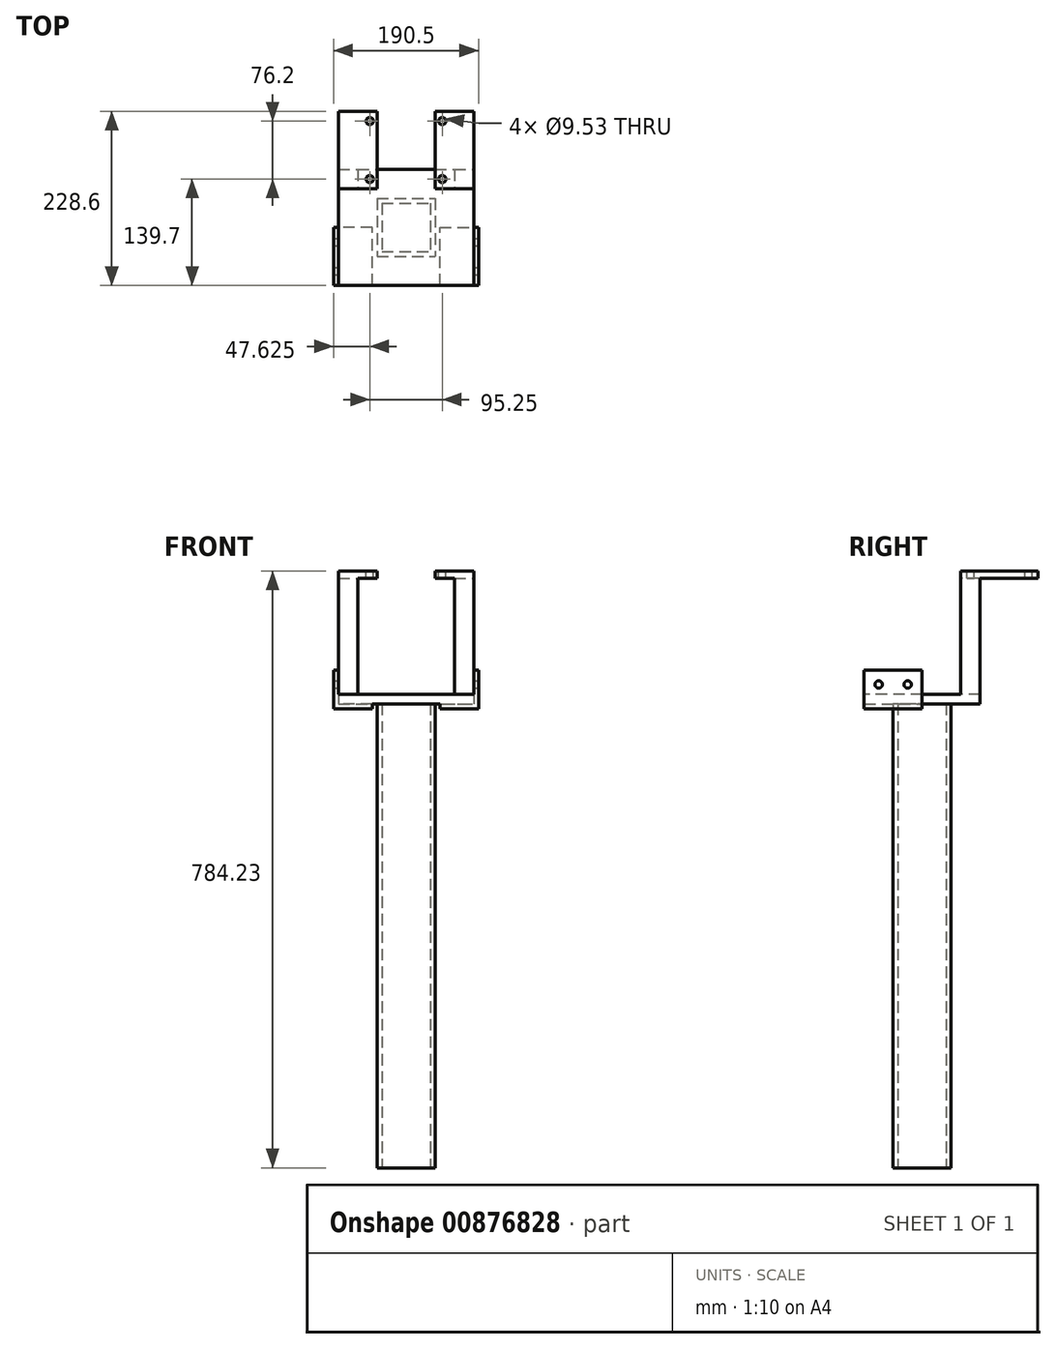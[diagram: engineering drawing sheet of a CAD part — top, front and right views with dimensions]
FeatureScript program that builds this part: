
annotation { "Feature Type Name" : "Feature", "Feature Type Description" : "" }
export const myFeature = defineFeature(function(context is Context, id is Id, definition is map)
    precondition{}
    {
        {
            var Q0;
            Q0=qCreatedBy(makeId("Top.planeOp"),FACE);
            var sketch = newSketch(context, id + "F0", { "sketchPlane" : qUnion([Q0])});
            skLineSegment(sketch, "E0.bottom", {"start": v(-38.1, 38.1) * mm, "end": v(38.1, 38.1) * mm});
            skLineSegment(sketch, "E0.top", {"start": v(-38.1, -38.1) * mm, "end": v(38.1, -38.1) * mm});
            skLineSegment(sketch, "E0.left", {"start": v(-38.1, 38.1) * mm, "end": v(-38.1, -38.1) * mm});
            skLineSegment(sketch, "E0.right", {"start": v(38.1, 38.1) * mm, "end": v(38.1, -38.1) * mm});
            skLineSegment(sketch, "E1.bottom", {"start": v(-31.75, 31.75) * mm, "end": v(31.75, 31.75) * mm});
            skLineSegment(sketch, "E1.top", {"start": v(-31.75, -31.75) * mm, "end": v(31.75, -31.75) * mm});
            skLineSegment(sketch, "E1.left", {"start": v(-31.75, 31.75) * mm, "end": v(-31.75, -31.75) * mm});
            skLineSegment(sketch, "E1.right", {"start": v(31.75, 31.75) * mm, "end": v(31.75, -31.75) * mm});
            skSolve(sketch);
        }
        {
            var Q0;
            Q0 = qSketchRegion(id + "F0", true);
            extrude(context, id + "F1", {"entities" : qUnion([Q0]), "depth" : 609.6 * mm, "offsetDistance" : 25.4 * mm});
        }
        {
            var Q0;
            Q0=makeQuery(id+"F1.opExtrude","CAP_FACE",FACE,{"disambiguationData":[OSD([sQuery(id+"F0.wireOp",EDGE,"E0.bottom"),sQuery(id+"F0.wireOp",EDGE,"E0.top"),sQuery(id+"F0.wireOp",EDGE,"E0.left"),sQuery(id+"F0.wireOp",EDGE,"E0.right"),sQuery(id+"F0.wireOp",EDGE,"E1.bottom"),sQuery(id+"F0.wireOp",EDGE,"E1.top"),sQuery(id+"F0.wireOp",EDGE,"E1.left"),sQuery(id+"F0.wireOp",EDGE,"E1.right")])],"isStart":false});
            var sketch = newSketch(context, id + "F2", { "sketchPlane" : qUnion([Q0])});
            skLineSegment(sketch, "E2.bottom", {"start": v(-88.9, 76.2) * mm, "end": v(88.9, 76.2) * mm});
            skLineSegment(sketch, "E2.top", {"start": v(-88.9, -76.2) * mm, "end": v(88.9, -76.2) * mm});
            skLineSegment(sketch, "E2.left", {"start": v(-88.9, 76.2) * mm, "end": v(-88.9, -76.2) * mm});
            skLineSegment(sketch, "E2.right", {"start": v(88.9, 76.2) * mm, "end": v(88.9, -76.2) * mm});
            skSolve(sketch);
        }
        {
            var Q0;
            Q0 = qSketchRegion(id + "F2", true);
            extrude(context, id + "F3", {"entities" : qUnion([Q0]), "operationType" : NewBodyOperationType.ADD, "depth" : 12.7 * mm, "offsetDistance" : 25.4 * mm});
        }
        {
            var Q0;
            {var subQ0=sQuery(id+"F2.wireOp",EDGE,"E2.top");var subQ1=sQuery(id+"F2.wireOp",EDGE,"E2.left");var subQ2=sQuery(id+"F2.wireOp",EDGE,"E2.bottom");var subQ3=sQuery(id+"F2.wireOp",EDGE,"E2.right");Q0=makeQuery(id+"F3.boolean.opBoolean","SPLIT",FACE,{"disambiguationData":[TD([makeQuery(id+"F1.opExtrude","SWEPT_FACE",FACE,{"disambiguationData":[OSD([sQuery(id+"F0.wireOp",EDGE,"E0.bottom")])]})])],"derivedFrom":makeQuery(id+"F3.opExtrude","CAP_FACE",FACE,{"disambiguationData":[OSD([subQ2,subQ0,subQ1,subQ3])],"isStart":true})});}
            var sketch = newSketch(context, id + "F4", { "sketchPlane" : qUnion([Q0])});
            skLineSegment(sketch, "E3", {"start": v(88.9, 76.2) * mm, "end": v(44.45, 76.2) * mm});
            skLineSegment(sketch, "E4", {"start": v(44.45, 76.2) * mm, "end": v(44.45, 0) * mm});
            skLineSegment(sketch, "E5", {"start": v(44.45, 0) * mm, "end": v(95.25, 0) * mm});
            skLineSegment(sketch, "E6", {"start": v(95.25, 0) * mm, "end": v(95.25, 76.2) * mm});
            skLineSegment(sketch, "E7", {"start": v(95.25, 76.2) * mm, "end": v(88.9, 76.2) * mm});
            skLineSegment(sketch, "E8", {"start": v(-88.9, 76.2) * mm, "end": v(-44.45, 76.2) * mm});
            skLineSegment(sketch, "E9", {"start": v(-44.45, 76.2) * mm, "end": v(-44.45, 0) * mm});
            skLineSegment(sketch, "E10", {"start": v(-44.45, 0) * mm, "end": v(-95.25, 0) * mm});
            skLineSegment(sketch, "E11", {"start": v(-95.25, 0) * mm, "end": v(-95.25, 76.2) * mm});
            skLineSegment(sketch, "E12", {"start": v(-95.25, 76.2) * mm, "end": v(-88.9, 76.2) * mm});
            skSolve(sketch);
        }
        {
            var Q0;
            Q0 = qSketchRegion(id + "F4", true);
            extrude(context, id + "F5", {"entities" : qUnion([Q0]), "operationType" : NewBodyOperationType.ADD, "depth" : 6.35 * mm, "offsetDistance" : 25.4 * mm});
        }
        {
            var Q0;
            Q0=makeQuery(id+"F5.opExtrude","CAP_FACE",FACE,{"disambiguationData":[OSD([sQuery(id+"F4.wireOp",EDGE,"E8"),sQuery(id+"F4.wireOp",EDGE,"E9"),sQuery(id+"F4.wireOp",EDGE,"E10"),sQuery(id+"F4.wireOp",EDGE,"E11"),sQuery(id+"F4.wireOp",EDGE,"E12")])],"isStart":true});
            var sketch = newSketch(context, id + "F6", { "sketchPlane" : qUnion([Q0])});
            skLineSegment(sketch, "E13", {"start": v(-95.25, 0) * mm, "end": v(-88.9, 0) * mm});
            skLineSegment(sketch, "E14", {"start": v(-88.9, 0) * mm, "end": v(-88.9, -76.2) * mm});
            skLineSegment(sketch, "E15", {"start": v(-88.9, -76.2) * mm, "end": v(-95.25, -76.2) * mm});
            skLineSegment(sketch, "E16", {"start": v(-95.25, -76.2) * mm, "end": v(-95.25, 0) * mm});
            skSolve(sketch);
        }
        {
            var Q0;
            Q0 = qSketchRegion(id + "F6", true);
            extrude(context, id + "F7", {"entities" : qUnion([Q0]), "operationType" : NewBodyOperationType.ADD, "depth" : 44.45 * mm, "offsetDistance" : 25.4 * mm});
        }
        {
            var Q0;
            Q0=makeQuery(id+"F5.opExtrude","CAP_FACE",FACE,{"disambiguationData":[OSD([sQuery(id+"F4.wireOp",EDGE,"E3"),sQuery(id+"F4.wireOp",EDGE,"E4"),sQuery(id+"F4.wireOp",EDGE,"E5"),sQuery(id+"F4.wireOp",EDGE,"E6"),sQuery(id+"F4.wireOp",EDGE,"E7")])],"isStart":true});
            var sketch = newSketch(context, id + "F8", { "sketchPlane" : qUnion([Q0])});
            skLineSegment(sketch, "E17", {"start": v(95.25, 0) * mm, "end": v(88.9, 0) * mm});
            skLineSegment(sketch, "E18", {"start": v(88.9, 0) * mm, "end": v(88.9, -76.2) * mm});
            skLineSegment(sketch, "E19", {"start": v(88.9, -76.2) * mm, "end": v(95.25, -76.2) * mm});
            skLineSegment(sketch, "E20", {"start": v(95.25, -76.2) * mm, "end": v(95.25, 0) * mm});
            skSolve(sketch);
        }
        {
            var Q0;
            Q0 = qSketchRegion(id + "F8", true);
            extrude(context, id + "F9", {"entities" : qUnion([Q0]), "operationType" : NewBodyOperationType.ADD, "depth" : 44.45 * mm, "offsetDistance" : 25.4 * mm});
        }
        {
            var Q0;
            Q0=makeQuery(id+"F9.boolean.opBoolean","MERGE",FACE,{"derivedFrom":[makeQuery(id+"F5.opExtrude","SWEPT_FACE",FACE,{"disambiguationData":[OSD([sQuery(id+"F4.wireOp",EDGE,"E6")])]}),makeQuery(id+"F9.opExtrude","SWEPT_FACE",FACE,{"disambiguationData":[OSD([sQuery(id+"F8.wireOp",EDGE,"E20")])]})]});
            var sketch = newSketch(context, id + "F10", { "sketchPlane" : qUnion([Q0])});
            skCircle(sketch, "E21", {"center": v(-57.15, 635) * mm, "radius": 4.76 * mm});
            skCircle(sketch, "E22", {"center": v(-19.05, 635) * mm, "radius": 4.76 * mm});
            skSolve(sketch);
        }
        {
            var Q0;
            Q0 = qSketchRegion(id + "F10", true);
            extrude(context, id + "F11", {"entities" : qUnion([Q0]), "operationType" : NewBodyOperationType.REMOVE, "oppositeDirection" : true, "depth" : 254 * mm, "offsetDistance" : 25.4 * mm});
        }
        {
            var Q0;
            Q0=makeQuery(id+"F3.opExtrude","CAP_FACE",FACE,{"disambiguationData":[OSD([sQuery(id+"F2.wireOp",EDGE,"E2.bottom"),sQuery(id+"F2.wireOp",EDGE,"E2.top"),sQuery(id+"F2.wireOp",EDGE,"E2.left"),sQuery(id+"F2.wireOp",EDGE,"E2.right")])],"isStart":false});
            var sketch = newSketch(context, id + "F12", { "sketchPlane" : qUnion([Q0])});
            skSolve(sketch);
        }
        {
            var Q0;
            {var subQ3=sQuery(id+"F2.wireOp",EDGE,"E2.bottom");Q0=makeQuery(id+"F12.imprint","IMPRINT",FACE,{"disambiguationData":[TD([[makeQuery(id+"F12.imprint","IMPRINT",EDGE,{"derivedFrom":makeQuery(id+"F3.opExtrude","CAP_EDGE",EDGE,{"disambiguationData":[OSD([subQ3])],"isStart":false})}),-1.0]])]});}
            var sketch = newSketch(context, id + "F13", { "sketchPlane" : qUnion([Q0])});
            skLineSegment(sketch, "E23", {"start": v(-88.9, 76.2) * mm, "end": v(-63.5, 76.2) * mm});
            skLineSegment(sketch, "E24", {"start": v(-63.5, 76.2) * mm, "end": v(-63.5, 50.8) * mm});
            skLineSegment(sketch, "E25", {"start": v(-63.5, 50.8) * mm, "end": v(-88.9, 50.8) * mm});
            skLineSegment(sketch, "E26", {"start": v(-88.9, 50.8) * mm, "end": v(-88.9, 76.2) * mm});
            skLineSegment(sketch, "E27", {"start": v(88.9, 76.2) * mm, "end": v(63.5, 76.2) * mm});
            skLineSegment(sketch, "E28", {"start": v(63.5, 76.2) * mm, "end": v(63.5, 50.8) * mm});
            skLineSegment(sketch, "E29", {"start": v(63.5, 50.8) * mm, "end": v(88.9, 50.8) * mm});
            skLineSegment(sketch, "E30", {"start": v(88.9, 50.8) * mm, "end": v(88.9, 76.2) * mm});
            skSolve(sketch);
        }
        {
            var Q0;
            Q0 = qSketchRegion(id + "F13", true);
            extrude(context, id + "F14", {"entities" : qUnion([Q0]), "operationType" : NewBodyOperationType.ADD, "depth" : 152.4 * mm, "offsetDistance" : 25.4 * mm});
        }
        {
            var Q0;
            Q0=makeQuery(id+"F14.opExtrude","CAP_FACE",FACE,{"disambiguationData":[OSD([sQuery(id+"F13.wireOp",EDGE,"E27"),sQuery(id+"F13.wireOp",EDGE,"E28"),sQuery(id+"F13.wireOp",EDGE,"E29"),sQuery(id+"F13.wireOp",EDGE,"E30")])],"isStart":false});
            var sketch = newSketch(context, id + "F15", { "sketchPlane" : qUnion([Q0])});
            skLineSegment(sketch, "E31", {"start": v(88.9, 50.8) * mm, "end": v(88.9, 152.4) * mm});
            skLineSegment(sketch, "E32", {"start": v(88.9, 152.4) * mm, "end": v(38.1, 152.4) * mm});
            skLineSegment(sketch, "E33", {"start": v(38.1, 152.4) * mm, "end": v(38.1, 50.8) * mm});
            skLineSegment(sketch, "E34", {"start": v(38.1, 50.8) * mm, "end": v(88.9, 50.8) * mm});
            skSolve(sketch);
        }
        {
            var Q0;
            Q0 = qSketchRegion(id + "F15", true);
            extrude(context, id + "F16", {"entities" : qUnion([Q0]), "operationType" : NewBodyOperationType.ADD, "depth" : 9.52 * mm, "offsetDistance" : 25.4 * mm});
        }
        {
            var Q0;
            Q0=makeQuery(id+"F14.opExtrude","CAP_FACE",FACE,{"disambiguationData":[OSD([sQuery(id+"F13.wireOp",EDGE,"E23"),sQuery(id+"F13.wireOp",EDGE,"E24"),sQuery(id+"F13.wireOp",EDGE,"E25"),sQuery(id+"F13.wireOp",EDGE,"E26")])],"isStart":false});
            var sketch = newSketch(context, id + "F17", { "sketchPlane" : qUnion([Q0])});
            skLineSegment(sketch, "E35", {"start": v(-88.9, 50.8) * mm, "end": v(-38.1, 50.8) * mm});
            skLineSegment(sketch, "E36", {"start": v(-38.1, 50.8) * mm, "end": v(-38.1, 152.4) * mm});
            skLineSegment(sketch, "E37", {"start": v(-38.1, 152.4) * mm, "end": v(-88.9, 152.4) * mm});
            skLineSegment(sketch, "E38", {"start": v(-88.9, 152.4) * mm, "end": v(-88.9, 50.8) * mm});
            skSolve(sketch);
        }
        {
            var Q0;
            Q0 = qSketchRegion(id + "F17", true);
            extrude(context, id + "F18", {"entities" : qUnion([Q0]), "operationType" : NewBodyOperationType.ADD, "depth" : 9.52 * mm, "offsetDistance" : 25.4 * mm});
        }
        {
            var Q0;
            Q0=makeQuery(id+"F18.opExtrude","CAP_FACE",FACE,{"disambiguationData":[OSD([sQuery(id+"F17.wireOp",EDGE,"E35"),sQuery(id+"F17.wireOp",EDGE,"E36"),sQuery(id+"F17.wireOp",EDGE,"E37"),sQuery(id+"F17.wireOp",EDGE,"E38")])],"isStart":false});
            var sketch = newSketch(context, id + "F19", { "sketchPlane" : qUnion([Q0])});
            skCircle(sketch, "E39", {"center": v(-47.62, 63.5) * mm, "radius": 4.76 * mm});
            skCircle(sketch, "E40", {"center": v(-47.62, 139.7) * mm, "radius": 4.76 * mm});
            skSolve(sketch);
        }
        {
            var Q0;
            Q0 = qSketchRegion(id + "F19", true);
            extrude(context, id + "F20", {"entities" : qUnion([Q0]), "operationType" : NewBodyOperationType.REMOVE, "oppositeDirection" : true, "depth" : 25.4 * mm, "offsetDistance" : 25.4 * mm});
        }
        {
            var Q0;
            Q0=makeQuery(id+"F16.opExtrude","CAP_FACE",FACE,{"disambiguationData":[OSD([sQuery(id+"F15.wireOp",EDGE,"E31"),sQuery(id+"F15.wireOp",EDGE,"E32"),sQuery(id+"F15.wireOp",EDGE,"E33"),sQuery(id+"F15.wireOp",EDGE,"E34")])],"isStart":false});
            var sketch = newSketch(context, id + "F21", { "sketchPlane" : qUnion([Q0])});
            skCircle(sketch, "E41", {"center": v(47.63, 63.5) * mm, "radius": 4.76 * mm});
            skCircle(sketch, "E42", {"center": v(47.63, 139.7) * mm, "radius": 4.76 * mm});
            skSolve(sketch);
        }
        {
            var Q0;
            Q0 = qSketchRegion(id + "F21", true);
            extrude(context, id + "F22", {"entities" : qUnion([Q0]), "operationType" : NewBodyOperationType.REMOVE, "oppositeDirection" : true, "depth" : 25.4 * mm, "offsetDistance" : 25.4 * mm});
        }
    });
